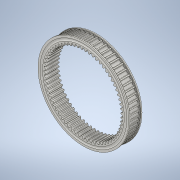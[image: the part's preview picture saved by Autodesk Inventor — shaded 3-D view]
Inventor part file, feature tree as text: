
AUTODESK INVENTOR PART (.ipt)
format: ipt  version: 2020 (Build 240168000, 168)  size: 1,217,536 bytes
history: native  units: mm (DEFAULTED — no unit token found)
features: sketch x5, extrude x4, plane x4, other x3, revolve x1, chamfer x1, mirror x1
ambient origin geometry x8: Origin, YZ Plane, XZ Plane, XY Plane, X Axis, Y Axis, Z Axis, Center Point
bodies: Solid1 (feature_tree)
feature tree (19):
  extrude  "Extrusion1"  Depth=14.0mm TaperAngle=0.0deg
  plane  "Work Plane1"
  plane  "Work Plane2"
  plane  "Work Plane3"
  other  "Spur Gear"
  sketch  "Sketch3"  dims[d6=0.0mm d7=0.490874mm d9=0.0mm]
  extrude  "Extrusion2"  Depth=76.2mm TaperAngle=0.0deg
  extrude  "Extrusion3"  TaperAngle=0.0deg  [1 undecoded]
  extrude  "Extrusion6"  TaperAngle=0.0deg  [1 undecoded]
  revolve  "Revolution1"  [1 undecoded]
  plane  "Work Plane4"
  chamfer  "Chamfer1"  Distance=91.34mm
  mirror  "Mirror1"
  sketch  "Sketch1"  dims[d0=92.9005mm d1=14.0mm d2=0.0mm]
  sketch  "Sketch2"  dims[d3=81.28mm d4=76.2mm d5=0.0mm]
  other  "Srf1"
  sketch  "Sketch4"  dims[d14=0.0mm d15=30.48mm d16=0.0mm]
  sketch  "Sketch6"  dims[d17=0.0mm d18=0.0mm d19=30.48mm d20=95.5mm d21=91.34mm d23=1.047198mm d24=3.05mm d25=0.86mm d26=600.0mm d28=360.0deg d30=25.4mm d31=0.0mm d32=25.4mm d33=0.0mm d34=0.01mm d35=0.01mm d38=0.8mm d43=1.5mm d44=0.0mm d45=3.175mm d46=45.0mm d47=0.79375mm d48=90.0deg d49=0.4mm d50=3.175mm d51=45.0deg]
  other  "Pitch Diameter"
note: 3 required parameter values undecoded (feature->parameter linkage not recoverable at this tier; creation-order binding heuristic only, values carry confidence <= 0.55)